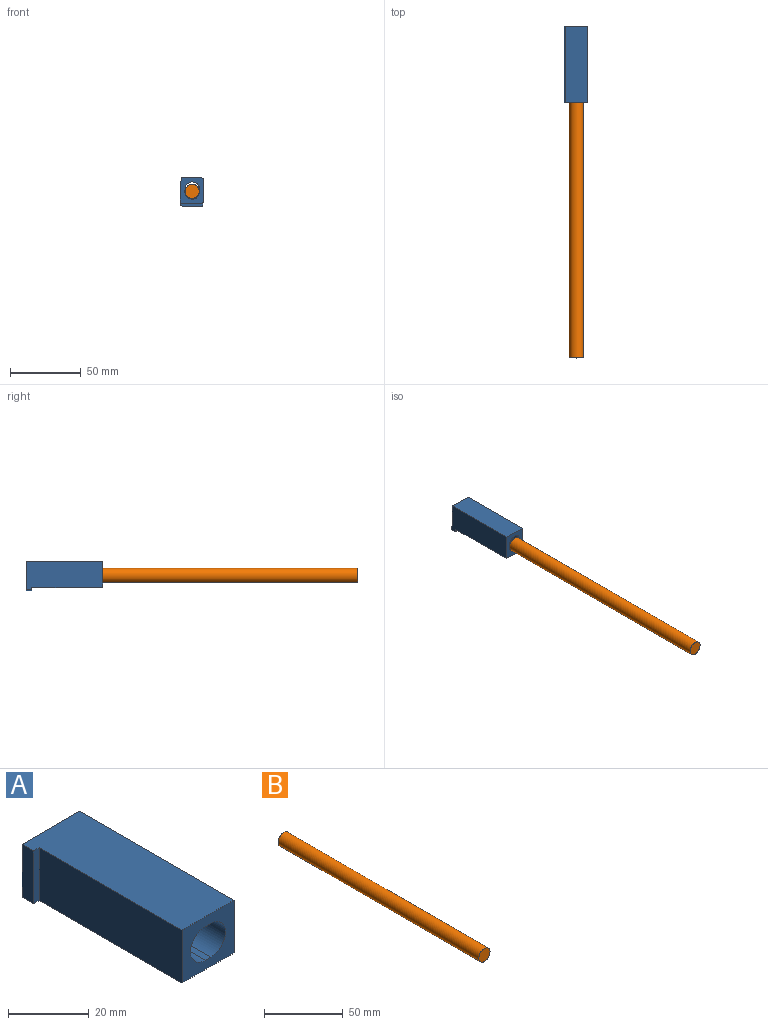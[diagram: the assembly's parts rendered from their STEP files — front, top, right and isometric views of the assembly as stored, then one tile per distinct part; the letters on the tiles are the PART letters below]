
ASSEMBLY  parts=2 mates=1
PART A: 12 faces, bbox 20.2x54x16 mm
  f0: plane 54x20.2mm, normal (0,0,1), area 990.8mm2, adj f2,f3,f4,f9,f10,f11
  f1: plane 54x20.2mm, normal (0,0,-1), area 990.8mm2, adj f2,f3,f4,f9,f10,f11
  f2: plane 20.2x16mm, normal (0,1,0), area 221.1mm2, adj f0,f1,f5,f6,f7,f8,f10,f11
  f3: plane 50x16mm, normal (-1,0,0), area 800mm2, adj f0,f1,f4,f9
  f4: plane 18.2x16mm, normal (0,-1,0), area 189.1mm2, adj f0,f1,f3,f5,f6,f7,f8,f10
  f5: cylinder r=5.1mm len=54mm, axis (0,1,0), area 865.2mm2, adj f2,f4,f6,f8
  f6: plane 54x2mm, normal (0,0,1), area 108mm2, adj f2,f4,f5,f7
  f7: cylinder r=5.1mm len=54mm, axis (0,1,0), area 865.2mm2, adj f2,f4,f6,f8
  f8: plane 54x2mm, normal (0,0,-1), area 108mm2, adj f2,f4,f5,f7
  f9: plane 16x2mm, normal (0,-1,0), area 32mm2, adj f0,f1,f3,f11
  f10: plane 54x16mm, normal (1,0,0), area 864mm2, adj f0,f1,f2,f4
  f11: plane 16x4mm, normal (-1,0,0), area 64mm2, adj f0,f1,f2,f9
PART B: 3 faces, bbox 10x180x10 mm
  f0: plane 10x10mm, normal (0,1,0), area 78.5mm2, adj f1
  f1: cylinder r=5mm len=180mm, axis (0,-1,0), area 5654.9mm2, adj f0,f2
  f2: plane 10x10mm, normal (0,-1,0), area 78.5mm2, adj f1
PLACE A rot(axis=(0,-1,0),88.1deg) t=(147.8,0,242.58)mm
PLACE B rot(axis=(0.92,0,0.39),180deg) t=(-133.86,-140,384.21)mm
MATE pin_slot B.f1 <-> A.f5  axis (0,1,0) through (-43.68,-50,204.17)mm
